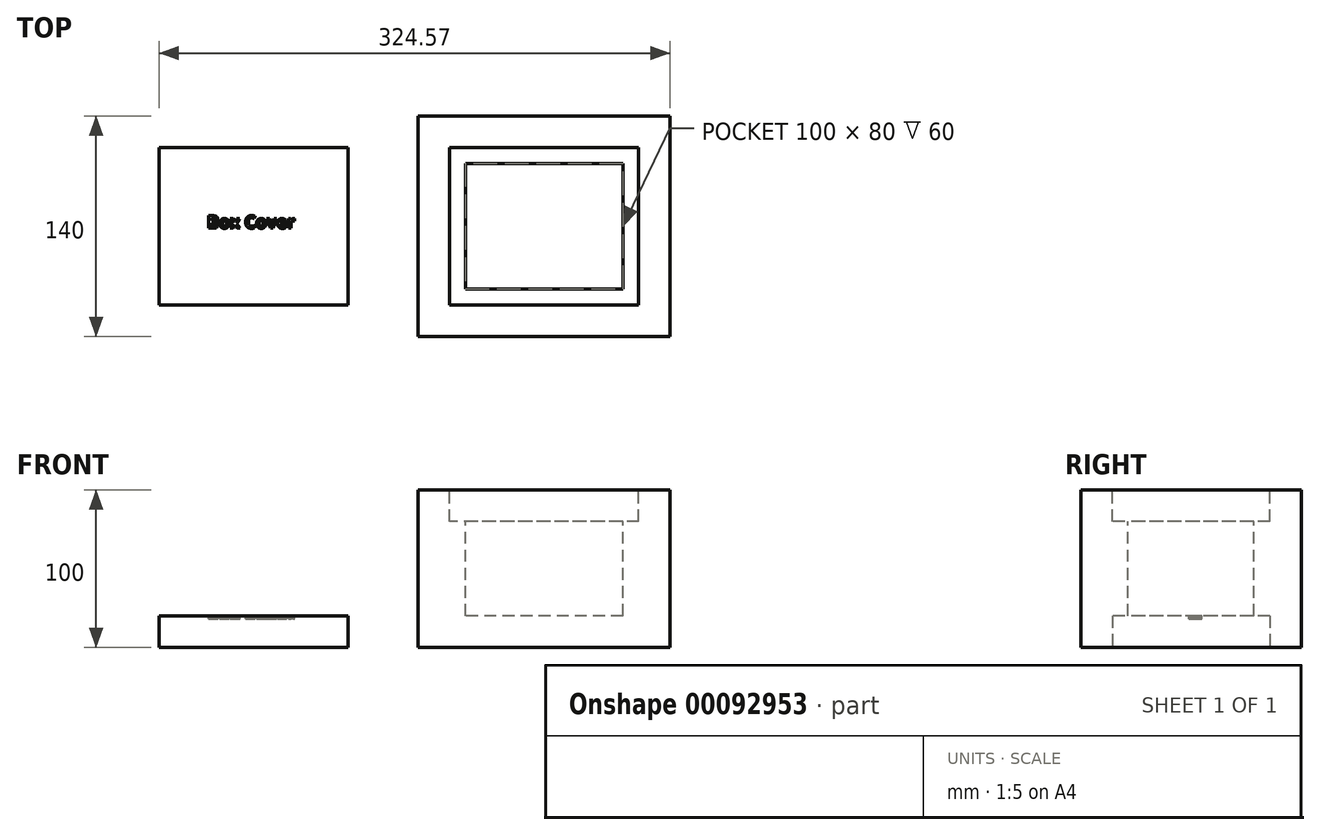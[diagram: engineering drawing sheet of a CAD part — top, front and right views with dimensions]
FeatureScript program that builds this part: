
annotation { "Feature Type Name" : "Feature", "Feature Type Description" : "" }
export const myFeature = defineFeature(function(context is Context, id is Id, definition is map)
    precondition{}
    {
        {
            var Q0;
            Q0=qCreatedBy(makeId("Top.planeOp"),FACE);
            var sketch = newSketch(context, id + "F0", { "sketchPlane" : qUnion([Q0])});
            skLineSegment(sketch, "E0.bottom", {"start": v(80, 70) * mm, "end": v(-80, 70) * mm});
            skLineSegment(sketch, "E0.top", {"start": v(80, -70) * mm, "end": v(-80, -70) * mm});
            skLineSegment(sketch, "E0.left", {"start": v(80, 70) * mm, "end": v(80, -70) * mm});
            skLineSegment(sketch, "E0.right", {"start": v(-80, 70) * mm, "end": v(-80, -70) * mm});
            skPoint(sketch, "E0.middle", {"position": v(0, 0) * mm});
            skSolve(sketch);
        }
        {
            var Q0;
            Q0 = qSketchRegion(id + "F0", true);
            extrude(context, id + "F1", {"entities" : qUnion([Q0]), "depth" : 100 * mm});
        }
        {
            var Q0;
            Q0=makeQuery(id+"F1.opExtrude","CAP_FACE",FACE,{"disambiguationData":[OSD([sQuery(id+"F0.wireOp",EDGE,"E0.bottom"),sQuery(id+"F0.wireOp",EDGE,"E0.top"),sQuery(id+"F0.wireOp",EDGE,"E0.left"),sQuery(id+"F0.wireOp",EDGE,"E0.right")])],"isStart":false});
            var sketch = newSketch(context, id + "F2", { "sketchPlane" : qUnion([Q0])});
            skLineSegment(sketch, "E1.bottom", {"start": v(60, 50) * mm, "end": v(-60, 50) * mm});
            skLineSegment(sketch, "E1.top", {"start": v(60, -50) * mm, "end": v(-60, -50) * mm});
            skLineSegment(sketch, "E1.left", {"start": v(60, 50) * mm, "end": v(60, -50) * mm});
            skLineSegment(sketch, "E1.right", {"start": v(-60, 50) * mm, "end": v(-60, -50) * mm});
            skPoint(sketch, "E1.middle", {"position": v(0, 0) * mm});
            skSolve(sketch);
        }
        {
            var Q0;
            Q0 = qSketchRegion(id + "F2", true);
            extrude(context, id + "F3", {"entities" : qUnion([Q0]), "operationType" : NewBodyOperationType.REMOVE, "oppositeDirection" : true, "depth" : 20 * mm});
        }
        {
            var Q0;
            Q0=makeQuery(id+"F3.boolean.opBoolean","COPY",FACE,{"derivedFrom":makeQuery(id+"F3.opExtrude","CAP_FACE",FACE,{"disambiguationData":[OSD([sQuery(id+"F2.wireOp",EDGE,"E1.bottom"),sQuery(id+"F2.wireOp",EDGE,"E1.top"),sQuery(id+"F2.wireOp",EDGE,"E1.left"),sQuery(id+"F2.wireOp",EDGE,"E1.right")])],"isStart":false})});
            var sketch = newSketch(context, id + "F4", { "sketchPlane" : qUnion([Q0])});
            skLineSegment(sketch, "E2.bottom", {"start": v(50, 40) * mm, "end": v(-50, 40) * mm});
            skLineSegment(sketch, "E2.top", {"start": v(50, -40) * mm, "end": v(-50, -40) * mm});
            skLineSegment(sketch, "E2.left", {"start": v(50, 40) * mm, "end": v(50, -40) * mm});
            skLineSegment(sketch, "E2.right", {"start": v(-50, 40) * mm, "end": v(-50, -40) * mm});
            skPoint(sketch, "E2.middle", {"position": v(0, 0) * mm});
            skSolve(sketch);
        }
        {
            var Q0;
            Q0 = qSketchRegion(id + "F4", true);
            extrude(context, id + "F5", {"entities" : qUnion([Q0]), "operationType" : NewBodyOperationType.REMOVE, "oppositeDirection" : true, "depth" : 60 * mm});
        }
        {
            var Q0;
            Q0=qCreatedBy(makeId("Top.planeOp"),FACE);
            var sketch = newSketch(context, id + "F6", { "sketchPlane" : qUnion([Q0])});
            skLineSegment(sketch, "E3.bottom", {"start": v(-124.57, 50) * mm, "end": v(-244.57, 50) * mm});
            skLineSegment(sketch, "E3.top", {"start": v(-124.57, -50) * mm, "end": v(-244.57, -50) * mm});
            skLineSegment(sketch, "E3.left", {"start": v(-124.57, 50) * mm, "end": v(-124.57, -50) * mm});
            skLineSegment(sketch, "E3.right", {"start": v(-244.57, 50) * mm, "end": v(-244.57, -50) * mm});
            skPoint(sketch, "E3.middle", {"position": v(-184.57, 0) * mm});
            skSolve(sketch);
        }
        {
            var Q0;
            Q0 = qSketchRegion(id + "F6", true);
            extrude(context, id + "F7", {"entities" : qUnion([Q0]), "depth" : 20 * mm});
        }
        {
            var Q0;
            Q0=makeQuery(id+"F7.opExtrude","CAP_FACE",FACE,{"disambiguationData":[OSD([sQuery(id+"F6.wireOp",EDGE,"E3.bottom"),sQuery(id+"F6.wireOp",EDGE,"E3.top"),sQuery(id+"F6.wireOp",EDGE,"E3.left"),sQuery(id+"F6.wireOp",EDGE,"E3.right")])],"isStart":false});
            var sketch = newSketch(context, id + "F8", { "sketchPlane" : qUnion([Q0])});
            skText(sketch, "E4", { "text": "Box Cover\n", "fontName": "OpenSans-Bold.ttf"});
            const initialGuessF8  = {"E4": [-0.21407, -0.00125, 1, 0, 0.00804]};
            skSetInitialGuess(sketch, initialGuessF8);
            skSolve(sketch);
        }
        {
            var Q0;
            Q0 = qSketchRegion(id + "F8", true);
            extrude(context, id + "F9", {"entities" : qUnion([Q0]), "operationType" : NewBodyOperationType.REMOVE, "oppositeDirection" : true, "depth" : 2 * mm});
        }
    });
